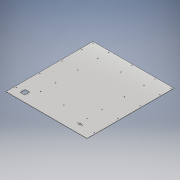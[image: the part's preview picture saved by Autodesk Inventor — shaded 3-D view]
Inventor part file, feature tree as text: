
AUTODESK INVENTOR PART (.ipt)
format: ipt  version: 2019 (Build 230136000, 136)  size: 249,344 bytes
history: native  units: mm
features: other x4, sketch x3, sheet_metal_op x1
ambient origin geometry x8: Origin, YZ Plane, XZ Plane, XY Plane, X Axis, Y Axis, Z Axis, Center Point
bodies: Body1 (feature_tree)
feature tree (8):
  sheet_metal_op  "Face5"
  sketch  "Sketch1"  dims[d0=513.0mm]
  other  "Plate5"
  sketch  "Sketch2"  dims[d1=550.0mm]
  sketch  "Sketch3"  dims[d2=10.0mm d3=10.0mm d4=10.0mm d5=110.0mm d6=80.0mm d7=110.0mm d8=110.0mm d9=70.0mm d10=55.0mm d11=4.2mm d12=0.8mm d13=0.8mm d16=0.8mm d19=0.8mm d20=0.8mm d21=1.5mm d22=32.0mm d23=28.0mm d24=36.0mm d25=3.4mm d26=50.0mm d28=1.5mm d29=0.0mm d30=56.0mm d31=56.0mm d32=30.0mm d33=11.25mm d34=12.0mm d35=3.5mm d36=100.0mm d37=1.5mm d38=0.0mm]
  other  "Cut1"
  other  "Cut2"
  other  "Definition1"
